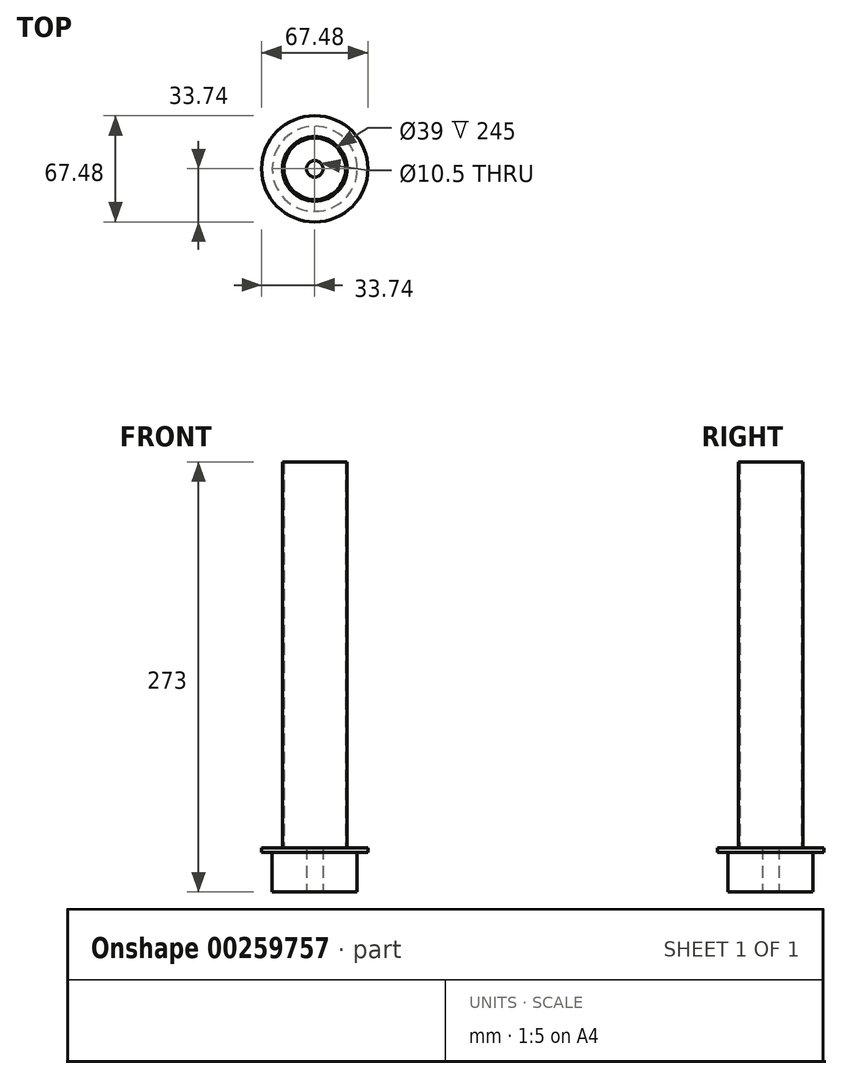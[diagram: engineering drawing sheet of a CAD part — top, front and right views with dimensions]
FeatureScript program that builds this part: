
annotation { "Feature Type Name" : "Feature", "Feature Type Description" : "" }
export const myFeature = defineFeature(function(context is Context, id is Id, definition is map)
    precondition{}
    {
        {
            var Q0;
            Q0=qCreatedBy(makeId("Top.planeOp"),FACE);
            var sketch = newSketch(context, id + "F0", { "sketchPlane" : qUnion([Q0])});
            skCircle(sketch, "E0", {"center": v(0, 0) * mm, "radius": 27 * mm});
            skCircle(sketch, "E1", {"center": v(0, 0) * mm, "radius": 5.25 * mm});
            skCircle(sketch, "E2", {"center": v(0, 0) * mm, "radius": 33.74 * mm});
            skSolve(sketch);
        }
        {
            var Q0;
            Q0=makeQuery(id+"F0.imprint","IMPRINT",FACE,{"disambiguationData":[TD([[makeQuery(id+"F0.imprint","IMPRINT",EDGE,{"derivedFrom":sQuery(id+"F0.wireOp",EDGE,"E0")}),-1.0]])]});
            var Q1;
            Q1=makeQuery(id+"F0.imprint","IMPRINT",FACE,{"disambiguationData":[TD([[makeQuery(id+"F0.imprint","IMPRINT",EDGE,{"derivedFrom":sQuery(id+"F0.wireOp",EDGE,"E0")}),1.0]])]});
            extrude(context, id + "F1", {"entities" : qUnion([Q0, Q1]), "depth" : 3 * mm});
        }
        {
            var Q0;
            Q0=makeQuery(id+"F0.imprint","IMPRINT",FACE,{"disambiguationData":[TD([[makeQuery(id+"F0.imprint","IMPRINT",EDGE,{"derivedFrom":sQuery(id+"F0.wireOp",EDGE,"E0")}),1.0]])]});
            var Q1;
            Q1=makeQuery(id+"F1.opExtrude","SWEPT_BODY",BODY,{"disambiguationData":[OSD([sQuery(id+"F0.wireOp",EDGE,"E0"),sQuery(id+"F0.wireOp",EDGE,"E2")])]});
            extrude(context, id + "F2", {"entities" : qUnion([Q0]), "operationType" : NewBodyOperationType.ADD, "oppositeDirection" : true, "endBoundEntityBody" : qUnion([Q1]), "depth" : 25 * mm});
        }
        {
            var Q0;
            Q0=makeQuery(id+"F1.opExtrude","CAP_FACE",FACE,{"disambiguationData":[OSD([sQuery(id+"F0.wireOp",EDGE,"E1"),sQuery(id+"F0.wireOp",EDGE,"E2")])],"isStart":false});
            var sketch = newSketch(context, id + "F3", { "sketchPlane" : qUnion([Q0])});
            skPoint(sketch, "E3.0", {"position": v(0, 0) * mm});
            skCircle(sketch, "E4", {"center": v(0, 0) * mm, "radius": 19.5 * mm});
            skCircle(sketch, "E5", {"center": v(0, 0) * mm, "radius": 20.5 * mm});
            skSolve(sketch);
        }
        {
            var Q0;
            Q0=makeQuery(id+"F3.imprint","IMPRINT",FACE,{"disambiguationData":[TD([[makeQuery(id+"F3.imprint","IMPRINT",EDGE,{"derivedFrom":sQuery(id+"F3.wireOp",EDGE,"E4")}),-1.0]])]});
            extrude(context, id + "F4", {"entities" : qUnion([Q0]), "depth" : 245 * mm});
        }
    });
